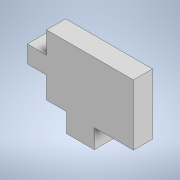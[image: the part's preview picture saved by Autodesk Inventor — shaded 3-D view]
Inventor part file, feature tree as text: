
AUTODESK INVENTOR PART (.ipt)
format: ipt  version: 2020 (Build 240168000, 168)  size: 112,128 bytes
history: native  units: mm
features: extrude x2, sketch x2
ambient origin geometry x8: Origin, YZ Plane, XZ Plane, XY Plane, X Axis, Y Axis, Z Axis, Center Point
bodies: Solide1 (feature_tree)
feature tree (4):
  extrude  "Extrusion1"  Depth=100.0mm
  extrude  "Extrusion2"  Depth=70.0mm TaperAngle=0.0deg
  sketch  "Esquisse1"
  sketch  "Esquisse2"
